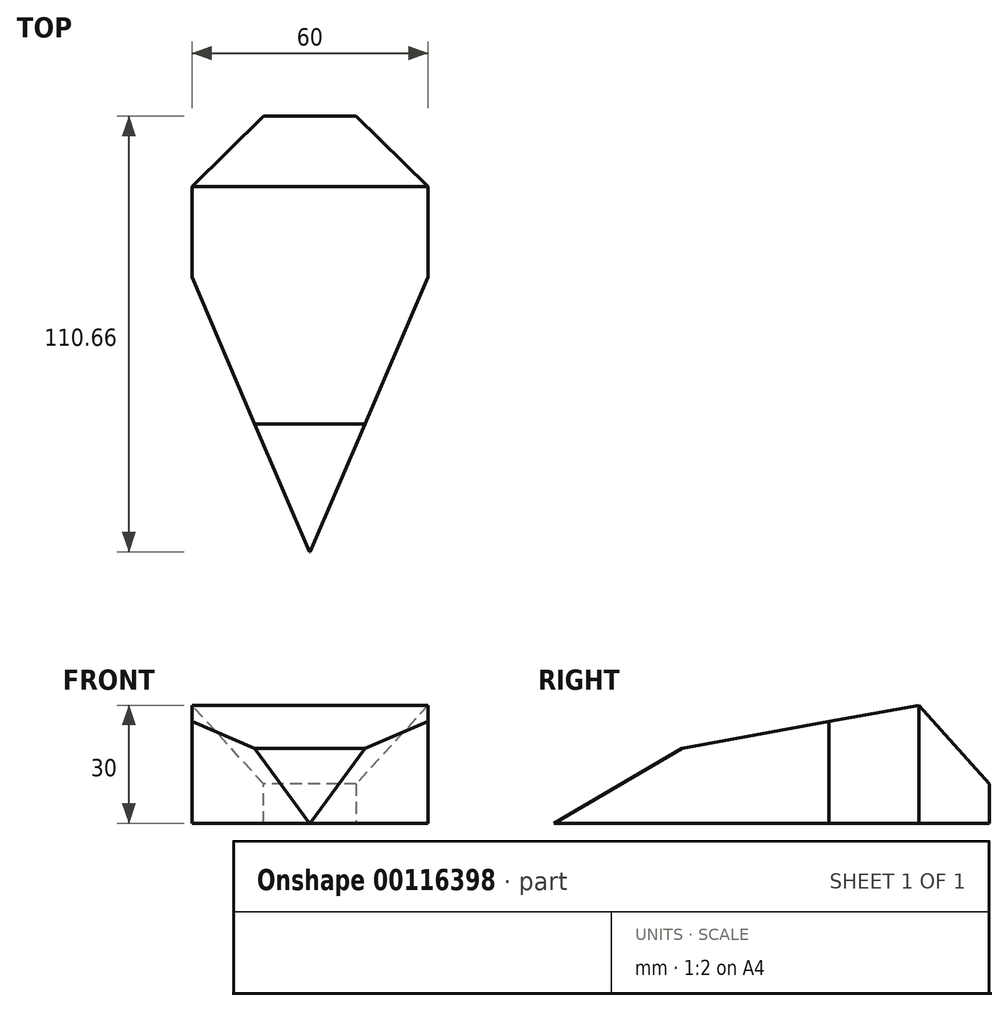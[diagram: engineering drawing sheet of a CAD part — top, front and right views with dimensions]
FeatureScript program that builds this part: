
annotation { "Feature Type Name" : "Feature", "Feature Type Description" : "" }
export const myFeature = defineFeature(function(context is Context, id is Id, definition is map)
    precondition{}
    {
        {
            var Q0;
            Q0=qCreatedBy(makeId("Right.planeOp"),FACE);
            var sketch = newSketch(context, id + "F0", { "sketchPlane" : qUnion([Q0])});
            skLineSegment(sketch, "E0", {"start": v(0, 0) * mm, "end": v(40.86, 0) * mm});
            skLineSegment(sketch, "E1", {"start": v(40.86, 0) * mm, "end": v(40.86, 10) * mm});
            skLineSegment(sketch, "E2", {"start": v(40.86, 10) * mm, "end": v(22.97, 10) * mm});
            skLineSegment(sketch, "E3", {"start": v(22.97, 10) * mm, "end": v(22.97, 30) * mm});
            skLineSegment(sketch, "E4", {"start": v(40.86, 10) * mm, "end": v(22.97, 30) * mm});
            skLineSegment(sketch, "E5", {"start": v(22.97, 30) * mm, "end": v(-37.29, 19.1) * mm});
            skLineSegment(sketch, "E6", {"start": v(-37.29, 19.1) * mm, "end": v(-69.8, 0) * mm});
            skLineSegment(sketch, "E7", {"start": v(40.86, 0) * mm, "end": v(-69.8, 0) * mm});
            skSolve(sketch);
        }
        {
            var Q0;
            Q0=makeQuery(id+"F0.imprint","IMPRINT",FACE,{"disambiguationData":[TD([[makeQuery(id+"F0.imprint","IMPRINT",EDGE,{"derivedFrom":sQuery(id+"F0.wireOp",EDGE,"E2")}),-1.0]])]});
            var Q1;
            {var subQ1=sQuery(id+"F0.wireOp",EDGE,"E1");Q1=makeQuery(id+"F0.imprint","IMPRINT",FACE,{"disambiguationData":[TD([[makeQuery(id+"F0.imprint","IMPRINT",EDGE,{"derivedFrom":subQ1}),1.0]])]});}
            extrude(context, id + "F1", {"entities" : qUnion([Q0, Q1]), "depth" : 30 * mm, "hasSecondDirection" : true, "secondDirectionOppositeDirection" : true, "secondDirectionDepth" : 30 * mm});
        }
        {
            var Q0;
            Q0=qCreatedBy(makeId("Top.planeOp"),FACE);
            var sketch = newSketch(context, id + "F2", { "sketchPlane" : qUnion([Q0])});
            skLineSegment(sketch, "E8", {"start": v(0, 42.57) * mm, "end": v(-10, 42.57) * mm});
            skLineSegment(sketch, "E9", {"start": v(0, 42.57) * mm, "end": v(10, 42.57) * mm});
            skLineSegment(sketch, "E10", {"start": v(0, 0) * mm, "end": v(-30, 0) * mm});
            skLineSegment(sketch, "E11", {"start": v(-10, 42.57) * mm, "end": v(-30, 22.97) * mm});
            skLineSegment(sketch, "E12", {"start": v(-30, 22.97) * mm, "end": v(-30, 0) * mm});
            skLineSegment(sketch, "E13", {"start": v(0, 0) * mm, "end": v(30, 0) * mm});
            skLineSegment(sketch, "E14", {"start": v(30, 22.97) * mm, "end": v(10, 42.57) * mm});
            skLineSegment(sketch, "E15", {"start": v(30, 22.97) * mm, "end": v(30, 0) * mm});
            skLineSegment(sketch, "E16", {"start": v(0, 0) * mm, "end": v(0, -70) * mm});
            skLineSegment(sketch, "E17", {"start": v(0, -70) * mm, "end": v(-30, 0) * mm});
            skLineSegment(sketch, "E18", {"start": v(0, -70) * mm, "end": v(30, 0) * mm});
            skLineSegment(sketch, "E19", {"start": v(-62.73, -77.39) * mm, "end": v(-62.73, 67.3) * mm});
            skLineSegment(sketch, "E20", {"start": v(-62.73, 67.3) * mm, "end": v(66.24, 67.3) * mm});
            skLineSegment(sketch, "E21", {"start": v(66.24, 67.3) * mm, "end": v(66.24, -77.39) * mm});
            skLineSegment(sketch, "E22", {"start": v(66.24, -77.39) * mm, "end": v(-62.73, -77.39) * mm});
            skSolve(sketch);
        }
        {
            var Q0;
            Q0=makeQuery(id+"F2.imprint","IMPRINT",FACE,{"disambiguationData":[TD([[makeQuery(id+"F2.imprint","IMPRINT",EDGE,{"derivedFrom":sQuery(id+"F2.wireOp",EDGE,"E8")}),-1.0]])]});
            var Q1;
            Q1 = qConstructionFilter(qBodyType(qCreatedBy(id + "F0" ,EDGE), BodyType.WIRE), ConstructionObject.NO);
            extrude(context, id + "F3", {"entities" : qUnion([Q0]), "operationType" : NewBodyOperationType.REMOVE, "surfaceEntities" : qUnion([Q1]), "depth" : 40 * mm});
        }
    });
